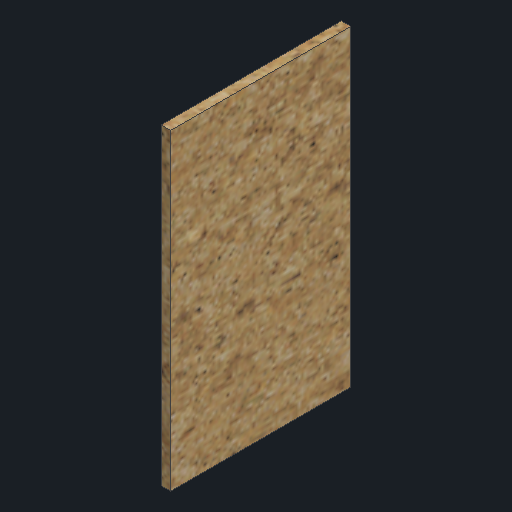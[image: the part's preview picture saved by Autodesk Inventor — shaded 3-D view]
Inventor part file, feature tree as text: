
AUTODESK INVENTOR PART (.ipt)
format: ipt  version: 2022 (Build 260153070, 153G)  size: 250,368 bytes
history: native  units: mm
features: other x1, extrude x1, sketch x1
ambient origin geometry x8: Origin, YZ Plane, XZ Plane, XY Plane, X Axis, Y Axis, Z Axis, Center Point
bodies: Body1 (feature_tree)
feature tree (3):
  other  "Твердое тело1"
  extrude  "Выдавливание1"  Depth=300.0mm
  sketch  "Эскиз2"
